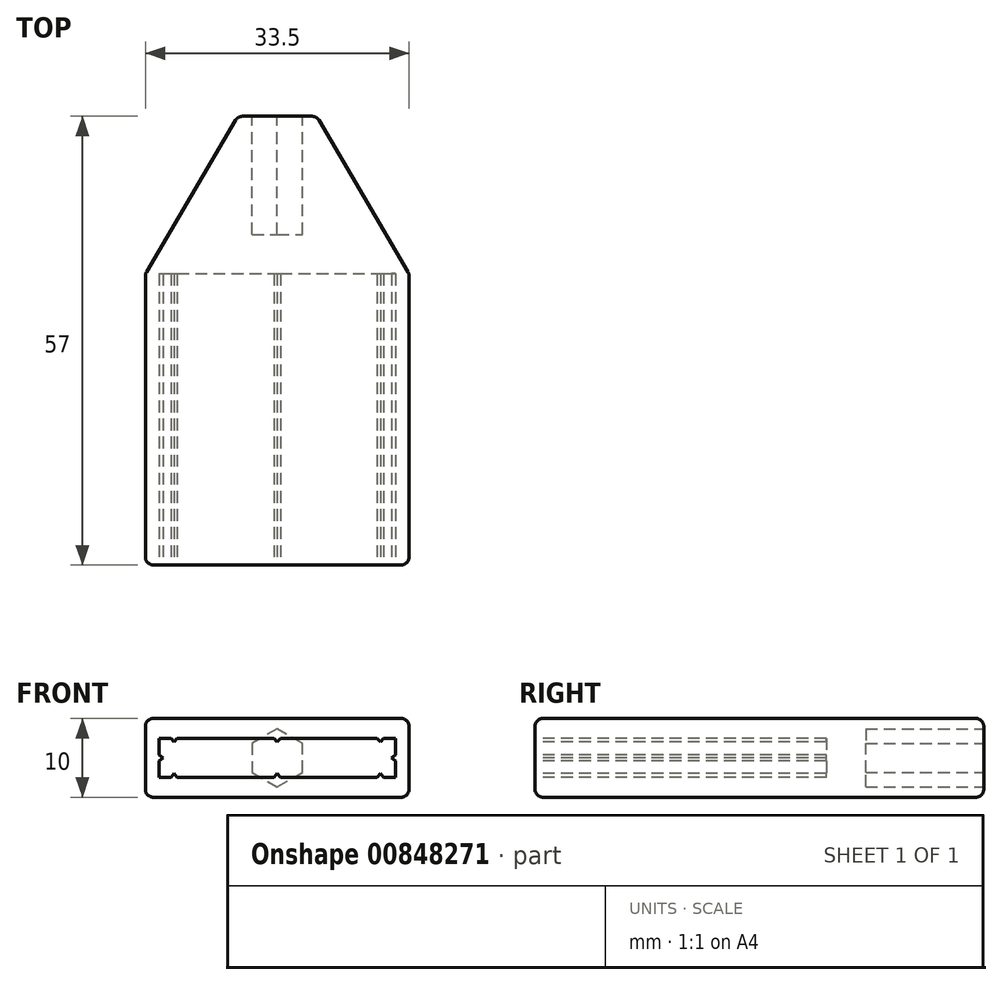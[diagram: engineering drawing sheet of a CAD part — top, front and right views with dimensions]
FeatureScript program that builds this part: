
annotation { "Feature Type Name" : "Feature", "Feature Type Description" : "" }
export const myFeature = defineFeature(function(context is Context, id is Id, definition is map)
    precondition{}
    {
        {
            var Q0;
            Q0=qCreatedBy(makeId("Top.planeOp"),FACE);
            var sketch = newSketch(context, id + "F0", { "sketchPlane" : qUnion([Q0])});
            skLineSegment(sketch, "E0.bottom", {"start": v(-16.75, 18.5) * mm, "end": v(16.75, 18.5) * mm});
            skLineSegment(sketch, "E0.top", {"start": v(-16.75, -18.5) * mm, "end": v(16.75, -18.5) * mm});
            skLineSegment(sketch, "E0.left", {"start": v(-16.75, 18.5) * mm, "end": v(-16.75, -18.5) * mm});
            skLineSegment(sketch, "E0.right", {"start": v(16.75, 18.5) * mm, "end": v(16.75, -18.5) * mm});
            skPoint(sketch, "E0.middle", {"position": v(0, 0) * mm});
            skLineSegment(sketch, "E1", {"start": v(-16.75, 18.5) * mm, "end": v(-5, 38.5) * mm});
            skLineSegment(sketch, "E2", {"start": v(-5, 38.5) * mm, "end": v(5, 38.5) * mm});
            skLineSegment(sketch, "E3", {"start": v(5, 38.5) * mm, "end": v(16.75, 18.5) * mm});
            skLineSegment(sketch, "E4", {"start": v(0, 0) * mm, "end": v(0, 38.29) * mm, "construction": true});
            skPoint(sketch, "E5", {"position": v(0, 38.5) * mm});
            skSolve(sketch);
        }
        {
            var Q0;
            Q0=makeQuery(id+"F0.imprint","IMPRINT",FACE,{"disambiguationData":[TD([[makeQuery(id+"F0.imprint","IMPRINT",EDGE,{"derivedFrom":sQuery(id+"F0.wireOp",EDGE,"E0.top")}),1.0]])]});
            extrude(context, id + "F1", {"entities" : qUnion([Q0]), "depth" : 10 * mm, "offsetDistance" : 25 * mm});
        }
        {
            var Q0;
            Q0=makeQuery(id+"F1.opExtrude","SWEPT_FACE",FACE,{"disambiguationData":[OSD([sQuery(id+"F0.wireOp",EDGE,"E0.top")])]});
            var sketch = newSketch(context, id + "F2", { "sketchPlane" : qUnion([Q0])});
            skLineSegment(sketch, "E6", {"start": v(-16.75, 5) * mm, "end": v(16.75, 5) * mm, "construction": true});
            skLineSegment(sketch, "E7.bottom", {"start": v(-15, 7.5) * mm, "end": v(15, 7.5) * mm});
            skLineSegment(sketch, "E7.top", {"start": v(-15, 2.5) * mm, "end": v(15, 2.5) * mm});
            skLineSegment(sketch, "E7.left", {"start": v(-15, 7.5) * mm, "end": v(-15, 2.5) * mm});
            skLineSegment(sketch, "E7.right", {"start": v(15, 7.5) * mm, "end": v(15, 2.5) * mm});
            skPoint(sketch, "E7.middle", {"position": v(0, 5) * mm});
            skLineSegment(sketch, "E8", {"start": v(0, 7.5) * mm, "end": v(0, 2.5) * mm, "construction": true});
            skLineSegment(sketch, "E9", {"start": v(-13.5, 2.5) * mm, "end": v(-13.1, 3) * mm});
            skLineSegment(sketch, "E10", {"start": v(-13.1, 3) * mm, "end": v(-12.7, 2.5) * mm});
            skLineSegment(sketch, "E11", {"start": v(-13.5, 2.5) * mm, "end": v(-12.7, 2.5) * mm});
            skLineSegment(sketch, "E12.MirrorCS", {"start": v(-13.5, 7.5) * mm, "end": v(-12.7, 7.5) * mm});
            skLineSegment(sketch, "E13.MirrorCS", {"start": v(-13.1, 7) * mm, "end": v(-12.7, 7.5) * mm});
            skLineSegment(sketch, "E14.MirrorCS", {"start": v(-13.5, 7.5) * mm, "end": v(-13.1, 7) * mm});
            skLineSegment(sketch, "E15.1.0.0", {"start": v(-0.4, 2.5) * mm, "end": v(0.4, 2.5) * mm});
            skLineSegment(sketch, "E15.1.0.1", {"start": v(-0.4, 2.5) * mm, "end": v(0, 3) * mm});
            skLineSegment(sketch, "E15.1.0.2", {"start": v(0, 3) * mm, "end": v(0.4, 2.5) * mm});
            skLineSegment(sketch, "E15.1.0.3", {"start": v(0, 7) * mm, "end": v(0.4, 7.5) * mm});
            skLineSegment(sketch, "E15.1.0.4", {"start": v(-0.4, 7.5) * mm, "end": v(0.4, 7.5) * mm});
            skLineSegment(sketch, "E15.1.0.5", {"start": v(-0.4, 7.5) * mm, "end": v(0, 7) * mm});
            skLineSegment(sketch, "E15.1.0.6", {"start": v(-1.9, 2.5) * mm, "end": v(28.1, 2.5) * mm});
            skLineSegment(sketch, "E15.2.0.0", {"start": v(12.7, 2.5) * mm, "end": v(13.5, 2.5) * mm});
            skLineSegment(sketch, "E15.2.0.1", {"start": v(12.7, 2.5) * mm, "end": v(13.1, 3) * mm});
            skLineSegment(sketch, "E15.2.0.2", {"start": v(13.1, 3) * mm, "end": v(13.5, 2.5) * mm});
            skLineSegment(sketch, "E15.2.0.3", {"start": v(13.1, 7) * mm, "end": v(13.5, 7.5) * mm});
            skLineSegment(sketch, "E15.2.0.4", {"start": v(12.7, 7.5) * mm, "end": v(13.5, 7.5) * mm});
            skLineSegment(sketch, "E15.2.0.5", {"start": v(12.7, 7.5) * mm, "end": v(13.1, 7) * mm});
            skLineSegment(sketch, "E15.2.0.6", {"start": v(11.2, 2.5) * mm, "end": v(41.2, 2.5) * mm});
            skLineSegment(sketch, "E15.direction1", {"start": v(-13.5, 2.5) * mm, "end": v(-0.4, 2.5) * mm, "construction": true});
            skLineSegment(sketch, "E16", {"start": v(-15, 5.4) * mm, "end": v(-14.5, 5) * mm});
            skLineSegment(sketch, "E17", {"start": v(-14.5, 5) * mm, "end": v(-15, 4.6) * mm});
            skLineSegment(sketch, "E18", {"start": v(-15, 4.6) * mm, "end": v(-15, 5.4) * mm});
            skLineSegment(sketch, "E19", {"start": v(-14.5, 5) * mm, "end": v(-15, 5) * mm, "construction": true});
            skLineSegment(sketch, "E20", {"start": v(-13.1, 3) * mm, "end": v(-13.1, 2.5) * mm, "construction": true});
            skLineSegment(sketch, "E21.MirrorCS", {"start": v(-15, 4.6) * mm, "end": v(-14.5, 5) * mm});
            skLineSegment(sketch, "E22.MirrorCS", {"start": v(-14.5, 5) * mm, "end": v(-15, 5.4) * mm});
            skLineSegment(sketch, "E23.MirrorCS", {"start": v(-15, 5.4) * mm, "end": v(-15, 4.6) * mm});
            skLineSegment(sketch, "E24.MirrorCS", {"start": v(0, 2.5) * mm, "end": v(0, 7.5) * mm, "construction": true});
            skLineSegment(sketch, "E25.MirrorCS", {"start": v(14.5, 5) * mm, "end": v(15, 5.4) * mm});
            skLineSegment(sketch, "E26.MirrorCS", {"start": v(15, 5.4) * mm, "end": v(15, 4.6) * mm});
            skLineSegment(sketch, "E27.MirrorCS", {"start": v(15, 4.6) * mm, "end": v(14.5, 5) * mm});
            skSolve(sketch);
        }
        {
            var Q0;
            Q0=makeQuery(id+"F2.imprint","IMPRINT",FACE,{"disambiguationData":[TD([[makeQuery(id+"F2.imprint","IMPRINT",EDGE,{"derivedFrom":sQuery(id+"F2.wireOp",EDGE,"E7.bottom")}),-1.0]])]});
            var Q1;
            Q1=makeQuery(id+"F1.opExtrude","SWEPT_FACE",FACE,{"disambiguationData":[OSD([sQuery(id+"F0.wireOp",EDGE,"E0.bottom")])]});
            extrude(context, id + "F3", {"entities" : qUnion([Q0]), "operationType" : NewBodyOperationType.REMOVE, "endBound" : BoundingType.UP_TO_SURFACE, "oppositeDirection" : true, "depth" : 25 * mm, "endBoundEntityFace" : qUnion([Q1]), "offsetDistance" : 25 * mm});
        }
        {
            var Q0;
            Q0=makeQuery(id+"F0.imprint","IMPRINT",FACE,{"disambiguationData":[TD([[makeQuery(id+"F0.imprint","IMPRINT",EDGE,{"derivedFrom":sQuery(id+"F0.wireOp",EDGE,"E0.bottom")}),1.0]])]});
            extrude(context, id + "F4", {"entities" : qUnion([Q0]), "operationType" : NewBodyOperationType.ADD, "depth" : 10 * mm, "offsetDistance" : 25 * mm});
        }
        {
            var Q0;
            Q0=makeQuery(id+"F4.opExtrude","SWEPT_FACE",FACE,{"disambiguationData":[OSD([sQuery(id+"F0.wireOp",EDGE,"E2")])]});
            var sketch = newSketch(context, id + "F5", { "sketchPlane" : qUnion([Q0])});
            skLineSegment(sketch, "E28", {"start": v(0, 0) * mm, "end": v(0, 10) * mm, "construction": true});
            skCircle(sketch, "E29.cCircle", {"center": v(0, 5) * mm, "radius": 3.2 * mm, "construction": true});
            skLineSegment(sketch, "E29.0", {"start": v(-3.2, 3.15) * mm, "end": v(-3.2, 6.85) * mm});
            skLineSegment(sketch, "E29.1", {"start": v(-3.2, 6.85) * mm, "end": v(0, 8.7) * mm});
            skLineSegment(sketch, "E29.2", {"start": v(0, 8.7) * mm, "end": v(3.2, 6.85) * mm});
            skLineSegment(sketch, "E29.3", {"start": v(3.2, 6.85) * mm, "end": v(3.2, 3.15) * mm});
            skLineSegment(sketch, "E29.4", {"start": v(3.2, 3.15) * mm, "end": v(0, 1.3) * mm});
            skLineSegment(sketch, "E29.5", {"start": v(0, 1.3) * mm, "end": v(-3.2, 3.15) * mm});
            skPoint(sketch, "E29.0.midPoint", {"position": v(-3.2, 5) * mm});
            skSolve(sketch);
        }
        {
            var Q0;
            Q0=makeQuery(id+"F5.imprint","IMPRINT",FACE,{"disambiguationData":[TD([[makeQuery(id+"F5.imprint","IMPRINT",EDGE,{"derivedFrom":sQuery(id+"F5.wireOp",EDGE,"E29.0")}),-1.0]])]});
            extrude(context, id + "F6", {"entities" : qUnion([Q0]), "operationType" : NewBodyOperationType.REMOVE, "oppositeDirection" : true, "depth" : 15 * mm, "offsetDistance" : 25 * mm});
        }
        {
            var Q0;
            {var subQ0=sQuery(id+"F0.wireOp",EDGE,"E0.bottom");Q0=makeQuery(id+"F4.boolean.opBoolean","MERGE",FACE,{"derivedFrom":[makeQuery(id+"F1.opExtrude","CAP_FACE",FACE,{"disambiguationData":[OSD([subQ0,sQuery(id+"F0.wireOp",EDGE,"E0.top"),sQuery(id+"F0.wireOp",EDGE,"E0.left"),sQuery(id+"F0.wireOp",EDGE,"E0.right")])],"isStart":false}),makeQuery(id+"F4.opExtrude","CAP_FACE",FACE,{"disambiguationData":[OSD([subQ0,sQuery(id+"F0.wireOp",EDGE,"E1"),sQuery(id+"F0.wireOp",EDGE,"E2"),sQuery(id+"F0.wireOp",EDGE,"E3")])],"isStart":false})]});}
            var Q1;
            {var subQ0=sQuery(id+"F0.wireOp",EDGE,"E0.bottom");Q1=makeQuery(id+"F4.boolean.opBoolean","MERGE",FACE,{"derivedFrom":[makeQuery(id+"F1.opExtrude","CAP_FACE",FACE,{"disambiguationData":[OSD([subQ0,sQuery(id+"F0.wireOp",EDGE,"E0.top"),sQuery(id+"F0.wireOp",EDGE,"E0.left"),sQuery(id+"F0.wireOp",EDGE,"E0.right")])],"isStart":true}),makeQuery(id+"F4.opExtrude","CAP_FACE",FACE,{"disambiguationData":[OSD([subQ0,sQuery(id+"F0.wireOp",EDGE,"E1"),sQuery(id+"F0.wireOp",EDGE,"E2"),sQuery(id+"F0.wireOp",EDGE,"E3")])],"isStart":true})]});}
            var Q2;
            Q2=makeQuery(id+"F1.opExtrude","SWEPT_FACE",FACE,{"disambiguationData":[OSD([sQuery(id+"F0.wireOp",EDGE,"E0.left")])]});
            var Q3;
            Q3=makeQuery(id+"F4.opExtrude","SWEPT_FACE",FACE,{"disambiguationData":[OSD([sQuery(id+"F0.wireOp",EDGE,"E1")])]});
            var Q4;
            Q4=makeQuery(id+"F4.opExtrude","SWEPT_FACE",FACE,{"disambiguationData":[OSD([sQuery(id+"F0.wireOp",EDGE,"E3")])]});
            var Q5;
            Q5=makeQuery(id+"F1.opExtrude","SWEPT_FACE",FACE,{"disambiguationData":[OSD([sQuery(id+"F0.wireOp",EDGE,"E0.right")])]});
            fillet(context, id + "F7", {"entities" : qUnion([Q0, Q1, Q2, Q3, Q4, Q5]), "radius" : 1 * mm, "tangentPropagation" : true, "allowEdgeOverflow" : false});
        }
    });
